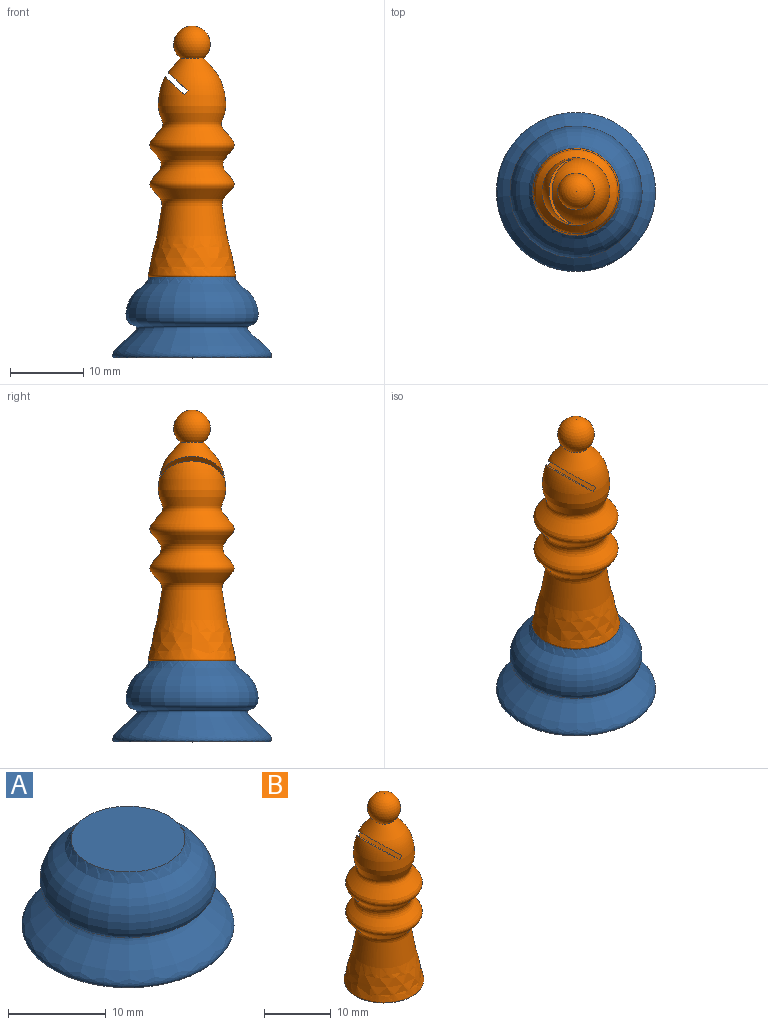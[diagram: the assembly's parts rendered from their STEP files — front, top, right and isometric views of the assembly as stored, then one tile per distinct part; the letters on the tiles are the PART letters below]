
ASSEMBLY  parts=2 mates=1
PART A: 3 faces, bbox 21.7x21.7x11 mm
  f0: plane 11.64x11.64mm, normal (0,0,1), area 106.4mm2, adj f1
  f1: revolved ~21.66x21.66mm, area 758.7mm2, adj f0,f2
  f2: cone r=10.76mm half-angle=89.7deg, axis (0,0,1), area 363.7mm2, adj f1
PART B: 6 faces, bbox 11.8x11.8x34.2 mm
  f0: sphere r=2.49mm, area 68.3mm2, adj f1
  f1: revolved ~29.82x11.8mm, area 964.1mm2, adj f0,f2,f3,f4,f5
  f2: plane 11.64x11.64mm, normal (0,0,-1), area 106.4mm2, adj f1
  f3: plane 8.65x2.73mm, normal (-0.68,0,-0.73), area 23.8mm2, adj f1,f5
  f4: plane 8.69x2.64mm, normal (0.68,0,0.73), area 22.8mm2, adj f1,f5
  f5: plane 8.71x0.54mm, normal (-0.73,0,0.68), area 6.3mm2, adj f1,f3,f4
PLACE A at identity
PLACE B t=(0,0,6.48)mm
MATE fastened B.f2 <-> A.f2  axis (0,0,-1) through (0,0,28.08)mm
